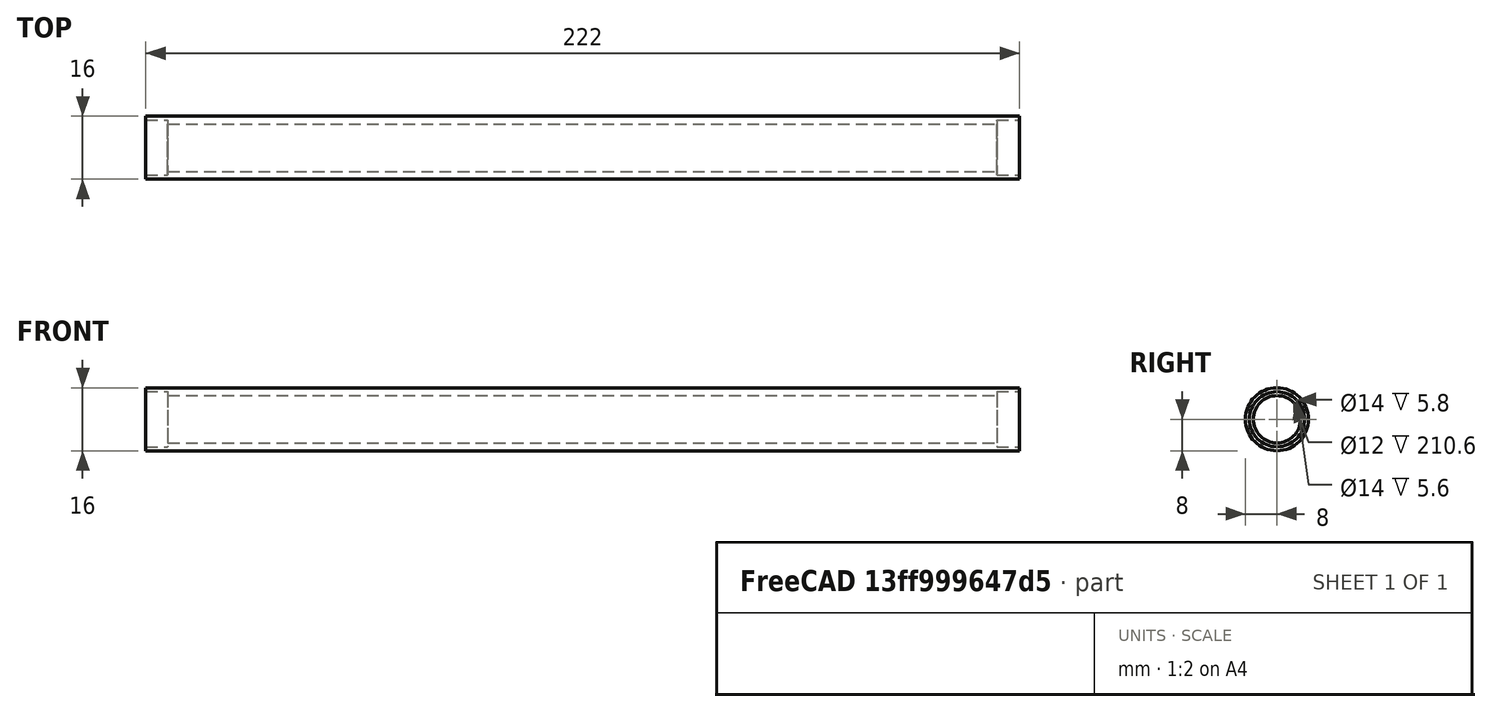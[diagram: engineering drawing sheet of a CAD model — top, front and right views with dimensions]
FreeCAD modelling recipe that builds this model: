
FCSTD DOCUMENT  (FreeCAD 0.21R38887 (Git))
Label: роликЗащитыY
License: All rights reserved
LicenseURL: http://en.wikipedia.org/wiki/All_rights_reserved
objects: Sketcher::SketchObject×1, PartDesign::Revolution×1, PartDesign::Body×1
note: 6 computed .brp shape members not serialized (recipe doc carries the construction recipe); baked Part::Feature solids carry a one-line shape summary decoded from their .brp
EXTERNAL_REF file=ТаблицаПараметров.FCStd obj=Spreadsheet002

FEATURE [Sketcher::SketchObject] Sketch
  ArcFitTolerance = 0
  AttachmentSupport = -> [XZ_Plane]
  ExternalBSplineMaxDegree = 0
  ExternalBSplineTolerance = 0
  FullyConstrained = true
  InternalTolerance = 1e-06
  InvalidShape = false
  MakeInternals = false
  MapMode = 5
  Placement = pos=(0,0,0) rot=(1,0,0;1.5708rad)
  Support = -> [XZ_Plane]
  TreeRank = 0
  ValidateShape = false
  expr: Constraints[19] = <<ТаблицаПараметров>>#<<Ролик>>.dimD3 / 2
  expr: Constraints[20] = (<<ТаблицаПараметров>>#<<Ролик>>.dimL1 - 2 * <<ТаблицаПараметров>>#<<Ролик>>.dimH3) / 2 + 0.4
  expr: Constraints[22] = (<<ТаблицаПараметров>>#<<Ролик>>.dimL1 - 2 * <<ТаблицаПараметров>>#<<Ролик>>.dimH3) / 2 + 0.2
  expr: Constraints[5] = <<ТаблицаПараметров>>#<<Ролик>>.dimD2 / 2
  expr: Constraints[6] = <<ТаблицаПараметров>>#<<Ролик>>.dimD1 / 2
  expr: Constraints[8] = <<ТаблицаПараметров>>#<<Ролик>>.dimL1
  expr: Constraints[9] = <<ТаблицаПараметров>>#<<Ролик>>.dimD2 / 2
  sketch-geometry (8):
    g0: LineSegment StartX=-111 StartY=8 StartZ=0 EndX=111 EndY=8 EndZ=0
    g1: LineSegment StartX=-111 StartY=7 StartZ=0 EndX=-105.4 EndY=7 EndZ=0
    g2: LineSegment StartX=-105.4 StartY=6 StartZ=0 EndX=105.2 EndY=6 EndZ=0
    g3: LineSegment StartX=105.2 StartY=6 StartZ=0 EndX=105.2 EndY=7 EndZ=0
    g4: LineSegment StartX=105.2 StartY=7 StartZ=0 EndX=111 EndY=7 EndZ=0
    g5: LineSegment StartX=-111 StartY=7 StartZ=0 EndX=-111 EndY=8 EndZ=0
    g6: LineSegment StartX=-105.4 StartY=6 StartZ=0 EndX=-105.4 EndY=7 EndZ=0
    g7: LineSegment StartX=111 StartY=7 StartZ=0 EndX=111 EndY=8 EndZ=0
  constraints (23):
    c: Horizontal(g1)
    c: Coincident(g3,g2)
    c: Vertical(g3)
    c: Horizontal(g4)
    c: Coincident(g3,g4)
    c: DistanceY(g-1,g1) = 7
    c: DistanceY(g0) = 8
    c: Symmetric(g0,g0,g-2)
    c: DistanceX(g0,g0) = 222
    c: DistanceY(g-1,g3) = 7
    c: Coincident(g5,g1)
    c: Coincident(g5,g0)
    c: Vertical(g5)
    c: Coincident(g6,g2)
    c: Coincident(g6,g1)
    c: Vertical(g6)
    c: Coincident(g7,g4)
    c: Coincident(g7,g0)
    c: Vertical(g7)
    c: DistanceY(g-1,g2) = 6
    c: DistanceX(g2,g-1) = 105.4
    c: Horizontal(g2)
    c: DistanceX(g-1,g2) = 105.2
FEATURE [PartDesign::Revolution] Revolution
  AddSubType = 0
  Angle = 360
  Axis = (1,0,0)
  Base = (0,0,0)
  ClaimChildren = false
  Fit = 0
  FitJoin = 0
  InnerFit = 0
  InnerFitJoin = 0
  InvalidShape = false
  NewSolid = false
  Placement = pos=(0,0,0) rot=(1,0,0;1.5708rad)
  Profile = -> Sketch
  ReferenceAxis = -> X_Axis
  Suppress = false
  TreeRank = 0
  ValidateShape = true
  _ProfileBasedVersion = 0
FEATURE [PartDesign::Body] Body  label="РоликТело"
  AutoGroupSolids = true
  ClaimAllChildren = false
  ExportMode = 0
  Group = -> [Sketch,Revolution]
  InvalidShape = false
  Origin = -> Origin
  Tip = -> Revolution
  TreeRank = 0
  ValidateShape = false
  _ExportChildren = -> [Revolution]
  _GroupVersion = 1
